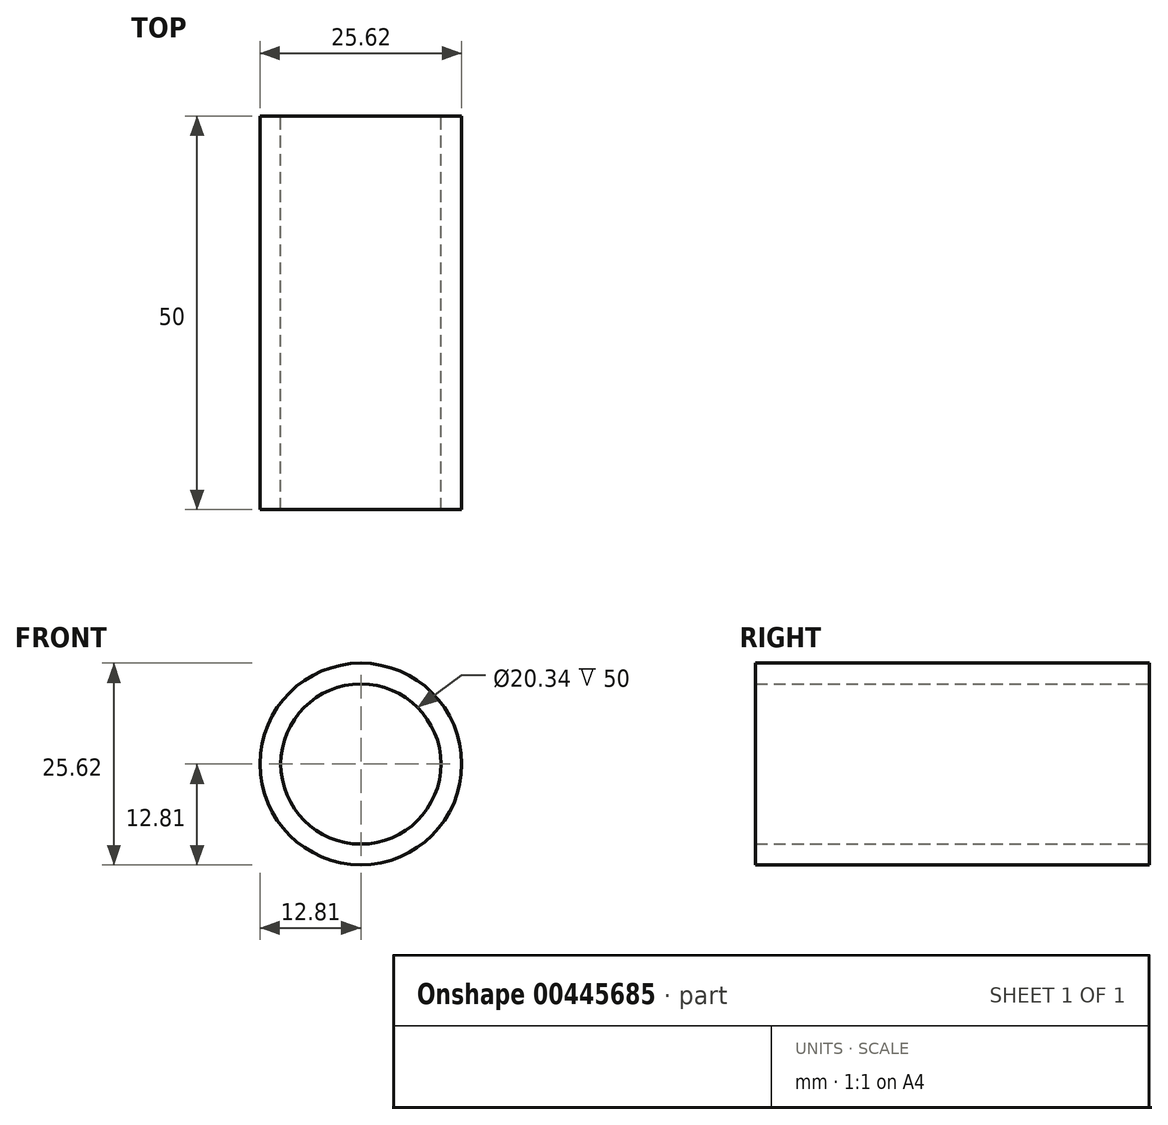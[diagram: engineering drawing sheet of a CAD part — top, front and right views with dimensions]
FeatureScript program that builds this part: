
annotation { "Feature Type Name" : "Feature", "Feature Type Description" : "" }
export const myFeature = defineFeature(function(context is Context, id is Id, definition is map)
    precondition{}
    {
        {
            var Q0;
            Q0=qCreatedBy(makeId("Front.planeOp"),FACE);
            var sketch = newSketch(context, id + "F0", { "sketchPlane" : qUnion([Q0])});
            skCircle(sketch, "E0", {"center": v(0, 0) * mm, "radius": 10.17 * mm});
            skCircle(sketch, "E1", {"center": v(0, 0) * mm, "radius": 12.8 * mm});
            skSolve(sketch);
        }
        {
            var Q0;
            Q0 = qSketchRegion(id + "F0", true);
            extrude(context, id + "F1", {"entities" : qUnion([Q0]), "depth" : 50 * mm});
        }
    });
